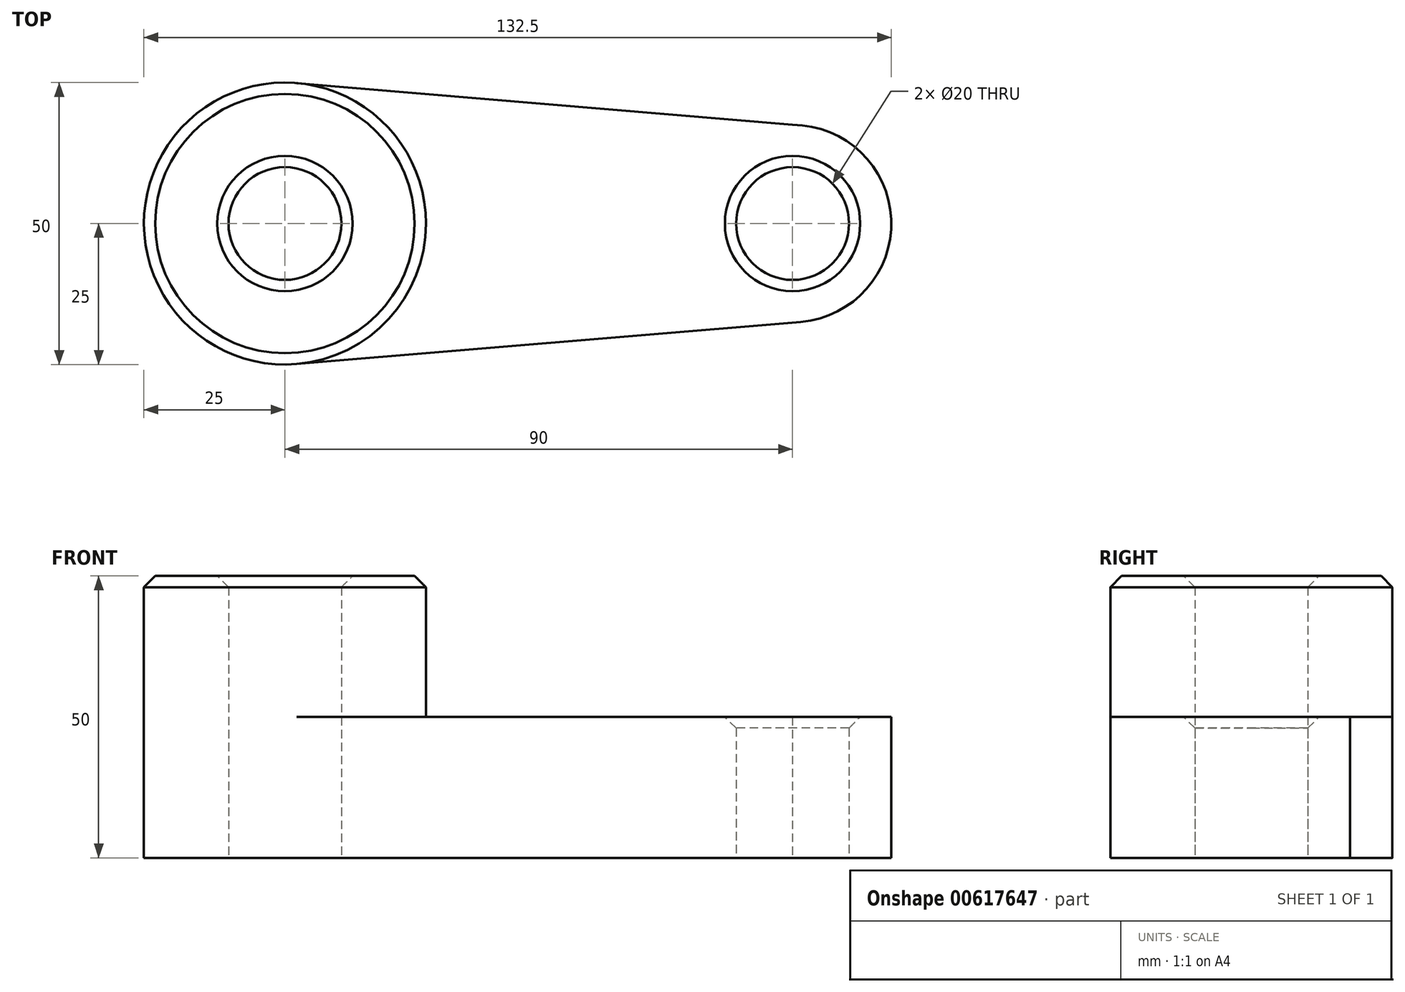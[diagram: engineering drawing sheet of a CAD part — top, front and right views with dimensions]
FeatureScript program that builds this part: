
annotation { "Feature Type Name" : "Feature", "Feature Type Description" : "" }
export const myFeature = defineFeature(function(context is Context, id is Id, definition is map)
    precondition{}
    {
        {
            var Q0;
            Q0=qCreatedBy(makeId("Top.planeOp"),FACE);
            var sketch = newSketch(context, id + "F0", { "sketchPlane" : qUnion([Q0])});
            skCircle(sketch, "E0", {"center": v(0, 0) * mm, "radius": 25 * mm});
            skCircle(sketch, "E1", {"center": v(90, 0) * mm, "radius": 17.5 * mm});
            skLineSegment(sketch, "E2", {"start": v(2.1, 24.91) * mm, "end": v(90, 17.5) * mm});
            skLineSegment(sketch, "E3", {"start": v(2.08, -24.91) * mm, "end": v(91.46, -17.44) * mm});
            skCircle(sketch, "E4", {"center": v(0, 0) * mm, "radius": 10 * mm});
            skCircle(sketch, "E5", {"center": v(90, 0) * mm, "radius": 10 * mm});
            skSolve(sketch);
        }
        {
            var Q0;
            Q0 = qSketchRegion(id + "F0", true);
            extrude(context, id + "F1", {"entities" : qUnion([Q0]), "depth" : 25 * mm, "offsetDistance" : 25 * mm});
        }
        {
            var Q0;
            Q0=makeQuery(id+"F0.imprint","IMPRINT",FACE,{"disambiguationData":[TD([[makeQuery(id+"F0.imprint","IMPRINT",EDGE,{"derivedFrom":sQuery(id+"F0.wireOp",EDGE,"E4")}),-1.0]])]});
            extrude(context, id + "F2", {"entities" : qUnion([Q0]), "operationType" : NewBodyOperationType.ADD, "depth" : 50 * mm, "offsetDistance" : 25 * mm});
        }
        {
            var Q0;
            Q0=makeQuery(id+"F2.opExtrude","CAP_EDGE",EDGE,{"disambiguationData":[OSD([sQuery(id+"F0.wireOp",EDGE,"E0")])],"isStart":false});
            var Q1;
            Q1=makeQuery(id+"F1.opExtrude","CAP_EDGE",EDGE,{"disambiguationData":[OSD([sQuery(id+"F0.wireOp",EDGE,"E5")])],"isStart":false});
            var Q2;
            Q2=makeQuery(id+"F2.opExtrude","CAP_EDGE",EDGE,{"disambiguationData":[OSD([sQuery(id+"F0.wireOp",EDGE,"E4")])],"isStart":false});
            chamfer(context, id + "F3", {"entities" : qUnion([Q0, Q1, Q2]), "width" : 2 * mm, "tangentPropagation" : true});
        }
    });
